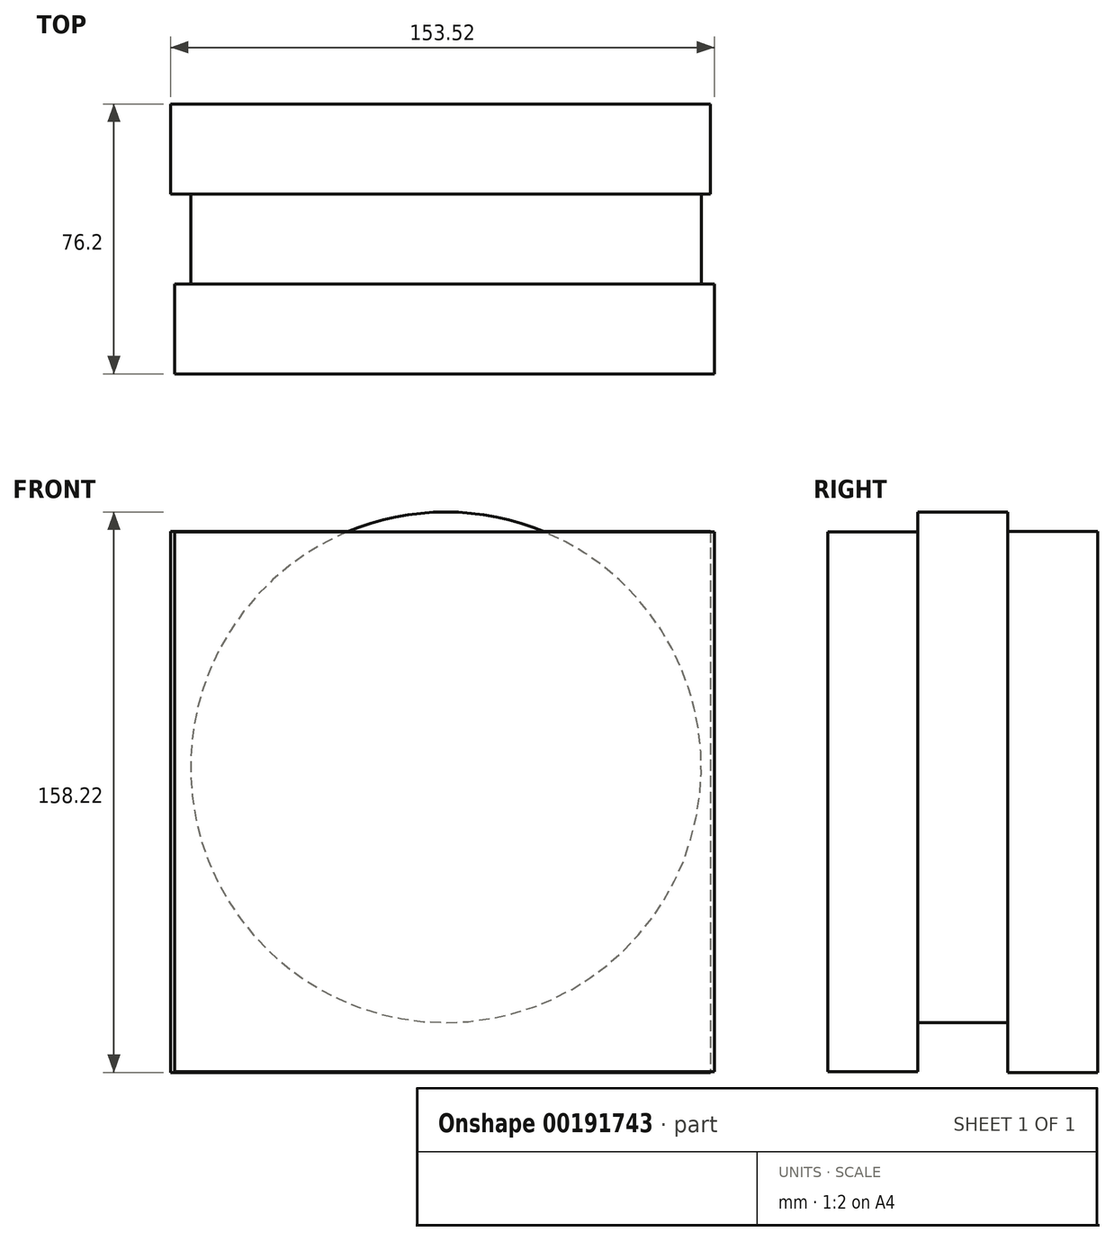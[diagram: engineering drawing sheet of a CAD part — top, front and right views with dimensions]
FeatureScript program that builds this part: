
annotation { "Feature Type Name" : "Feature", "Feature Type Description" : "" }
export const myFeature = defineFeature(function(context is Context, id is Id, definition is map)
    precondition{}
    {
        {
            var Q0;
            Q0=qCreatedBy(makeId("Front.planeOp"),FACE);
            var sketch = newSketch(context, id + "F0", { "sketchPlane" : qUnion([Q0])});
            skLineSegment(sketch, "E0.bottom", {"start": v(-76.6, 66.42) * mm, "end": v(75.8, 66.42) * mm});
            skLineSegment(sketch, "E0.top", {"start": v(-76.6, -85.98) * mm, "end": v(75.8, -85.98) * mm});
            skLineSegment(sketch, "E0.left", {"start": v(-76.6, 66.42) * mm, "end": v(-76.6, -85.98) * mm});
            skLineSegment(sketch, "E0.right", {"start": v(75.8, 66.42) * mm, "end": v(75.8, -85.98) * mm});
            skSolve(sketch);
        }
        {
            var Q0;
            Q0 = qSketchRegion(id + "F0", true);
            var Q1;
            Q1=makeQuery(id+"F0.imprint","IMPRINT",FACE,{"disambiguationData":[TD([[makeQuery(id+"F0.imprint","IMPRINT",EDGE,{"derivedFrom":sQuery(id+"F0.wireOp",EDGE,"E0.bottom")}),-1.0]])]});
            extrude(context, id + "F1", {"entities" : qUnion([Q0, Q1]), "depth" : 25.4 * mm});
        }
        {
            var Q0;
            Q0=makeQuery(id+"F1.opExtrude","CAP_FACE",FACE,{"disambiguationData":[OSD([sQuery(id+"F0.wireOp",EDGE,"E0.bottom"),sQuery(id+"F0.wireOp",EDGE,"E0.top"),sQuery(id+"F0.wireOp",EDGE,"E0.left"),sQuery(id+"F0.wireOp",EDGE,"E0.right")])],"isStart":true});
            var sketch = newSketch(context, id + "F2", { "sketchPlane" : qUnion([Q0])});
            skCircle(sketch, "E1", {"center": v(0, 0) * mm, "radius": 72.07 * mm});
            skSolve(sketch);
        }
        {
            var Q0;
            Q0 = qSketchRegion(id + "F2", true);
            extrude(context, id + "F3", {"entities" : qUnion([Q0]), "operationType" : NewBodyOperationType.ADD, "depth" : 25.4 * mm});
        }
        {
            var Q0;
            Q0=makeQuery(id+"F3.opExtrude","CAP_FACE",FACE,{"disambiguationData":[OSD([sQuery(id+"F2.wireOp",EDGE,"E1")])],"isStart":false});
            var sketch = newSketch(context, id + "F4", { "sketchPlane" : qUnion([Q0])});
            skLineSegment(sketch, "E2.bottom", {"start": v(-74.67, 66.6) * mm, "end": v(77.73, 66.6) * mm});
            skLineSegment(sketch, "E2.top", {"start": v(-74.67, -86.15) * mm, "end": v(77.73, -86.15) * mm});
            skLineSegment(sketch, "E2.left", {"start": v(-74.67, 66.6) * mm, "end": v(-74.67, -86.15) * mm});
            skLineSegment(sketch, "E2.right", {"start": v(77.73, 66.6) * mm, "end": v(77.73, -86.15) * mm});
            skSolve(sketch);
        }
        {
            var Q0;
            Q0 = qSketchRegion(id + "F4", true);
            extrude(context, id + "F5", {"entities" : qUnion([Q0]), "operationType" : NewBodyOperationType.ADD, "depth" : 25.4 * mm});
        }
    });
